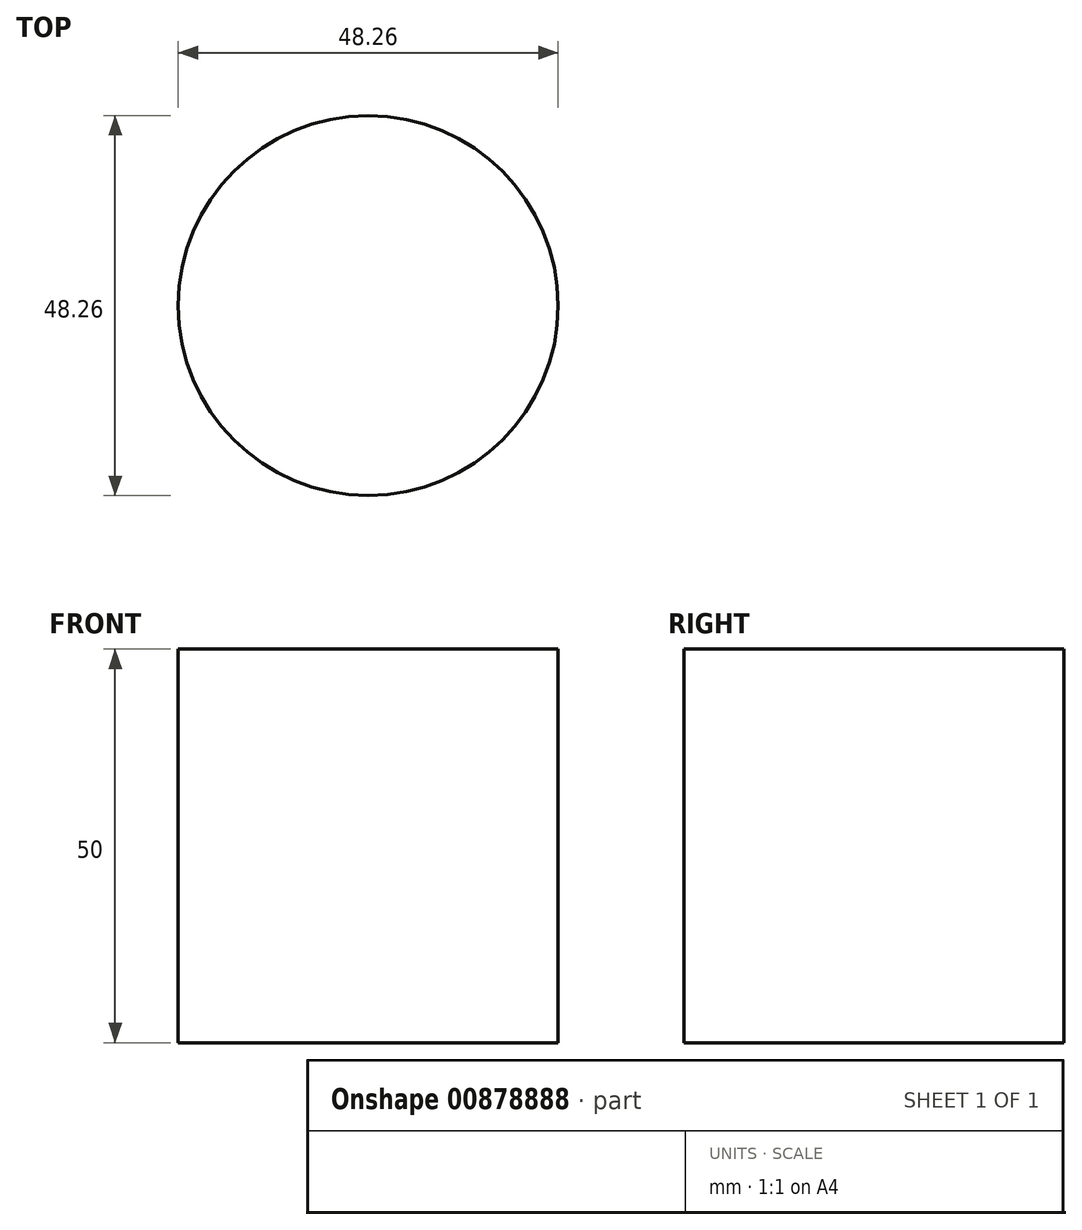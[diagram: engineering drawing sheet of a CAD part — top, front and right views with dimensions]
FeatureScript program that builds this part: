
annotation { "Feature Type Name" : "Feature", "Feature Type Description" : "" }
export const myFeature = defineFeature(function(context is Context, id is Id, definition is map)
    precondition{}
    {
        {
            var Q0;
            Q0=qCreatedBy(makeId("Top.planeOp"),FACE);
            var sketch = newSketch(context, id + "F0", { "sketchPlane" : qUnion([Q0])});
            skCircle(sketch, "E0", {"center": v(0, 0) * mm, "radius": 24.13 * mm});
            skSolve(sketch);
        }
        {
            var Q0;
            Q0 = qSketchRegion(id + "F0", true);
            extrude(context, id + "F1", {"entities" : qUnion([Q0]), "depth" : 50 * mm, "offsetDistance" : 25 * mm});
        }
    });
